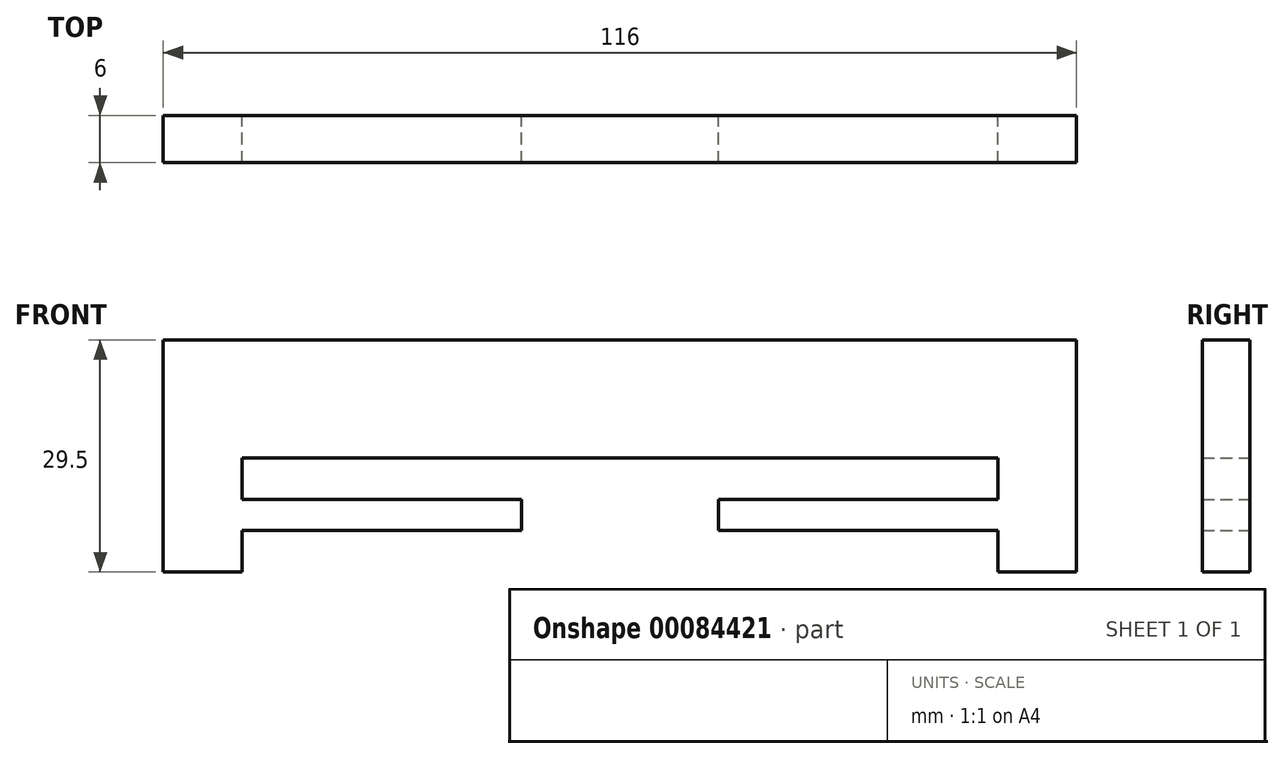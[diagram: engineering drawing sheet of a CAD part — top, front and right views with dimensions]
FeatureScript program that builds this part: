
annotation { "Feature Type Name" : "Feature", "Feature Type Description" : "" }
export const myFeature = defineFeature(function(context is Context, id is Id, definition is map)
    precondition{}
    {
        {
            var Q0;
            Q0=qCreatedBy(makeId("Front.planeOp"),FACE);
            var sketch = newSketch(context, id + "F0", { "sketchPlane" : qUnion([Q0])});
            skLineSegment(sketch, "E0", {"start": v(-58, 0) * mm, "end": v(-48, 0) * mm});
            skLineSegment(sketch, "E1.0", {"start": v(-48, 5.3) * mm, "end": v(-12.5, 5.3) * mm});
            skLineSegment(sketch, "E2.0", {"start": v(-48, 14.5) * mm, "end": v(48, 14.5) * mm});
            skLineSegment(sketch, "E3.0", {"start": v(-48, 9.2) * mm, "end": v(-12.5, 9.2) * mm});
            skLineSegment(sketch, "E4", {"start": v(0, 0) * mm, "end": v(0, 14.5) * mm});
            skLineSegment(sketch, "E5.0", {"start": v(48, 0) * mm, "end": v(48, 5.3) * mm});
            skLineSegment(sketch, "E6.0", {"start": v(-48, 0) * mm, "end": v(-48, 5.3) * mm});
            skLineSegment(sketch, "E7.0", {"start": v(-58, 0) * mm, "end": v(-58, 29.5) * mm});
            skLineSegment(sketch, "E8.0", {"start": v(58, 0) * mm, "end": v(58, 29.5) * mm});
            skLineSegment(sketch, "E9.trimOffspring", {"start": v(48, 0) * mm, "end": v(58, 0) * mm});
            skLineSegment(sketch, "E10.0", {"start": v(12.5, 5.3) * mm, "end": v(12.5, 9.2) * mm});
            skLineSegment(sketch, "E11.0", {"start": v(-12.5, 5.3) * mm, "end": v(-12.5, 9.2) * mm});
            skLineSegment(sketch, "E12.0", {"start": v(-58, 29.5) * mm, "end": v(58, 29.5) * mm});
            skLineSegment(sketch, "E13.trimOffspring", {"start": v(12.5, 9.2) * mm, "end": v(48, 9.2) * mm});
            skLineSegment(sketch, "E14.trimOffspring", {"start": v(12.5, 5.3) * mm, "end": v(48, 5.3) * mm});
            skLineSegment(sketch, "E15.trimOffspring", {"start": v(-48, 9.2) * mm, "end": v(-48, 14.5) * mm});
            skLineSegment(sketch, "E16.trimOffspring", {"start": v(48, 9.2) * mm, "end": v(48, 14.5) * mm});
            skSolve(sketch);
        }
        {
            var Q0;
            Q0=makeQuery(id+"F0.imprint","IMPRINT",FACE,{"disambiguationData":[TD([[makeQuery(id+"F0.imprint","IMPRINT",EDGE,{"derivedFrom":sQuery(id+"F0.wireOp",EDGE,"E0")}),1.0]])]});
            extrude(context, id + "F1", {"entities" : qUnion([Q0]), "depth" : 6 * mm});
        }
    });
